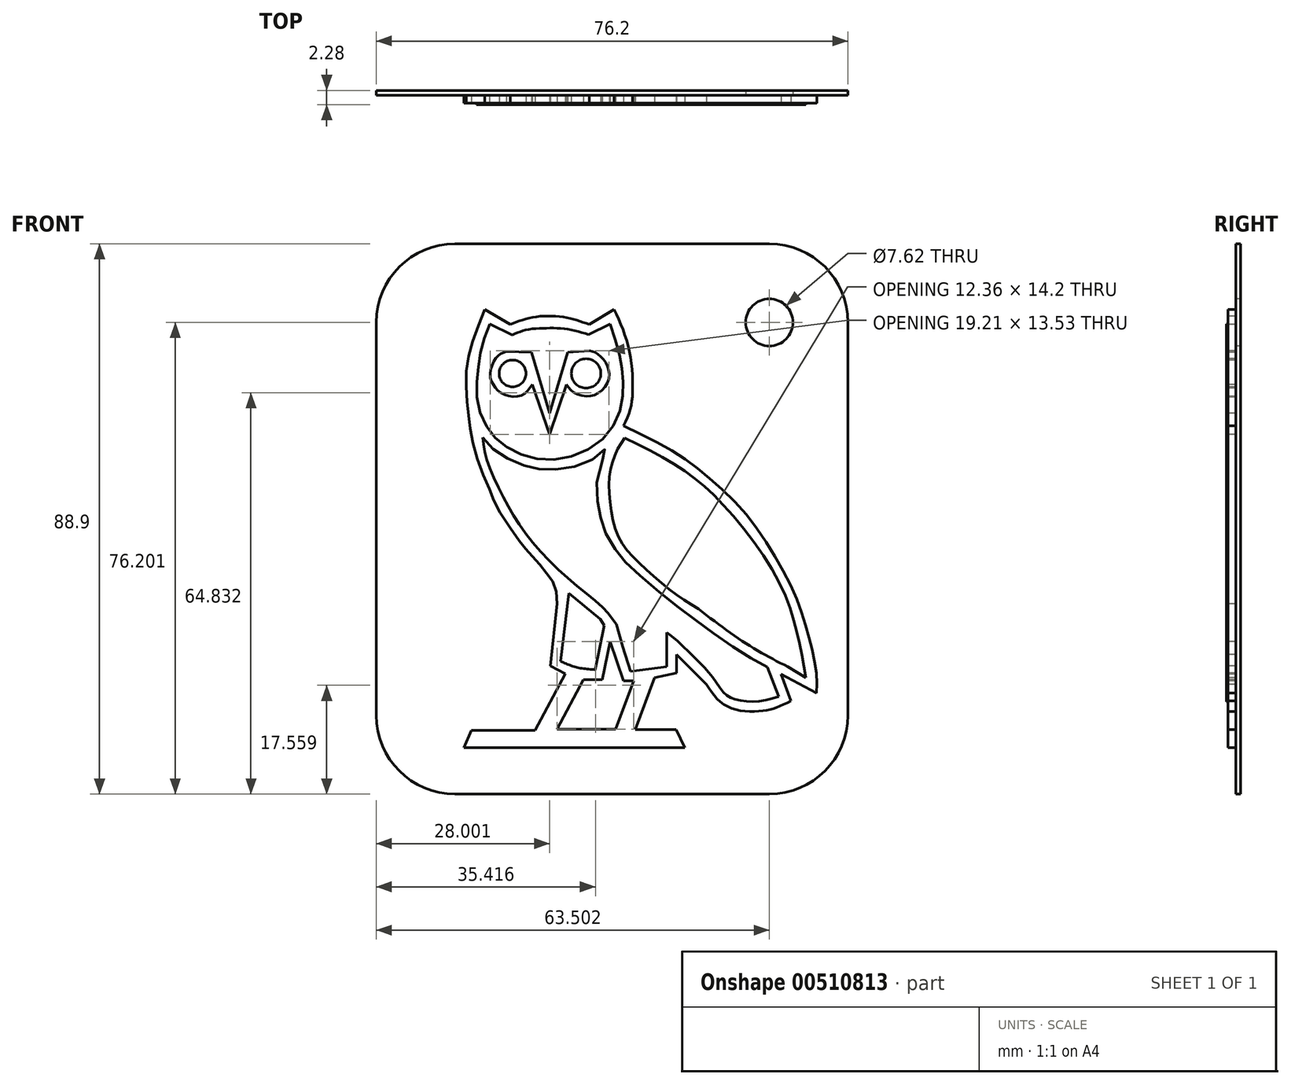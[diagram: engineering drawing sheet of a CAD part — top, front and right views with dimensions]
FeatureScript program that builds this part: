
annotation { "Feature Type Name" : "Feature", "Feature Type Description" : "" }
export const myFeature = defineFeature(function(context is Context, id is Id, definition is map)
    precondition{}
    {
        {
            var Q0;
            Q0=qCreatedBy(makeId("Front.planeOp"),FACE);
            var sketch = newSketch(context, id + "F0", { "sketchPlane" : qUnion([Q0])});
            skLineSegment(sketch, "E0", {"start": v(-23.6, -33.47) * mm, "end": v(12.06, -33.47) * mm});
            skLineSegment(sketch, "E1", {"start": v(12.06, -33.47) * mm, "end": v(10.65, -30.56) * mm});
            skLineSegment(sketch, "E2", {"start": v(10.65, -30.56) * mm, "end": v(4.09, -30.56) * mm});
            skLineSegment(sketch, "E3", {"start": v(4.09, -30.56) * mm, "end": v(7.18, -22.2) * mm});
            skLineSegment(sketch, "E4", {"start": v(7.18, -22.2) * mm, "end": v(10.75, -21.46) * mm});
            skLineSegment(sketch, "E5", {"start": v(10.75, -21.46) * mm, "end": v(10.75, -18.46) * mm});
            skLineSegment(sketch, "E6", {"start": v(10.75, -18.46) * mm, "end": v(15.53, -23.24) * mm});
            skFitSpline(sketch, "E7", {"points": [v(15.53, -23.24) * mm, v(17.79, -26.06) * mm, v(20.88, -27.46) * mm, v(24.54, -27.56) * mm, v(26.7, -27.09) * mm, v(29.23, -25.96) * mm], "startDerivative": vector(9.5, -14.38) * mm, "endDerivative": vector(13.86, 6.72) * mm});
            skLineSegment(sketch, "E8", {"start": v(29.23, -25.96) * mm, "end": v(27.64, -21.65) * mm});
            skLineSegment(sketch, "E9", {"start": v(27.64, -21.65) * mm, "end": v(33.36, -24.65) * mm});
            skFitSpline(sketch, "E10", {"points": [v(33.36, -24.65) * mm, v(33.36, -21.97) * mm, v(32.74, -18.12) * mm, v(31.6, -13.8) * mm, v(29.83, -8.64) * mm, v(26.36, -2.12) * mm, v(21.78, 4.45) * mm, v(15.74, 10.29) * mm, v(10.3, 14.34) * mm, v(2.15, 18.5) * mm], "startDerivative": vector(1.45, 34.65) * mm, "endDerivative": vector(-63.63, 29.95) * mm});
            skLineSegment(sketch, "E11", {"start": v(-3.39, 34.89) * mm, "end": v(0.66, 37.34) * mm});
            skLineSegment(sketch, "E12", {"start": v(0.66, 37.34) * mm, "end": v(-3.39, 34.89) * mm});
            skLineSegment(sketch, "E13", {"start": v(-20.24, 37.34) * mm, "end": v(-16.13, 34.89) * mm});
            skFitSpline(sketch, "E14", {"points": [v(-16.13, 34.89) * mm, v(-12.28, 36.08) * mm, v(-7.17, 36.01) * mm, v(-3.39, 34.89) * mm], "startDerivative": vector(11.3, 4.48) * mm, "endDerivative": vector(11.2, -4.14) * mm});
            skFitSpline(sketch, "E15", {"points": [v(0.66, 37.34) * mm, v(2.36, 33.28) * mm, v(3.44, 28.54) * mm, v(3.63, 23.85) * mm, v(3.25, 21.13) * mm, v(2.15, 18.5) * mm], "startDerivative": vector(8.55, -18.57) * mm, "endDerivative": vector(-7.4, -15.37) * mm});
            skLineSegment(sketch, "E16", {"start": v(-23.6, -33.47) * mm, "end": v(-22.43, -30.72) * mm});
            skLineSegment(sketch, "E17", {"start": v(-22.43, -30.72) * mm, "end": v(-12.15, -30.72) * mm});
            skLineSegment(sketch, "E18", {"start": v(-12.15, -30.72) * mm, "end": v(-7.24, -21.57) * mm});
            skLineSegment(sketch, "E19", {"start": v(-7.24, -21.57) * mm, "end": v(-9.66, -20.27) * mm});
            skLineSegment(sketch, "E20", {"start": v(-9.66, -20.27) * mm, "end": v(-8.53, -10.26) * mm});
            skFitSpline(sketch, "E21", {"points": [v(-8.53, -10.26) * mm, v(-8.96, -7.36) * mm, v(-10.18, -5.38) * mm, v(-11.77, -3.46) * mm, v(-13.41, -1.63) * mm, v(-14.68, 0) * mm, v(-18.09, 5.02) * mm, v(-19.43, 8.09) * mm, v(-21.5, 13.22) * mm, v(-22.6, 18.13) * mm, v(-23.04, 21.93) * mm, v(-23.24, 26.9) * mm, v(-22.37, 31.55) * mm, v(-20.24, 37.34) * mm], "startDerivative": vector(-2.62, 46.1) * mm, "endDerivative": vector(24.41, 61.36) * mm});
            skLineSegment(sketch, "E22", {"start": v(-8.53, -30.52) * mm, "end": v(0.9, -30.52) * mm});
            skLineSegment(sketch, "E23", {"start": v(0.9, -30.52) * mm, "end": v(3.83, -22.7) * mm});
            skLineSegment(sketch, "E24", {"start": v(3.83, -22.7) * mm, "end": v(2.17, -22.7) * mm});
            skLineSegment(sketch, "E25", {"start": v(2.17, -22.7) * mm, "end": v(0, -16.32) * mm});
            skLineSegment(sketch, "E26", {"start": v(0, -16.32) * mm, "end": v(-1.28, -22.5) * mm});
            skLineSegment(sketch, "E27", {"start": v(-1.28, -22.5) * mm, "end": v(-4.33, -22.5) * mm});
            skLineSegment(sketch, "E28", {"start": v(-4.33, -22.5) * mm, "end": v(-8.53, -30.52) * mm});
            skLineSegment(sketch, "E29", {"start": v(-6.68, -8.56) * mm, "end": v(-7.98, -19.53) * mm});
            skFitSpline(sketch, "E30", {"points": [v(-7.98, -19.53) * mm, v(-5.57, -20.48) * mm, v(-2.38, -20.9) * mm], "startDerivative": vector(4.87, -2.28) * mm, "endDerivative": vector(6.31, -0.51) * mm});
            skLineSegment(sketch, "E31", {"start": v(-2.38, -20.9) * mm, "end": v(-0.92, -13.77) * mm});
            skFitSpline(sketch, "E32", {"points": [v(-0.92, -13.77) * mm, v(-1.59, -12.7) * mm], "startDerivative": vector(-0.67, 1.07) * mm, "endDerivative": vector(-0.67, 1.07) * mm});
            skLineSegment(sketch, "E33", {"start": v(-1.59, -12.7) * mm, "end": v(-6.68, -8.56) * mm});
            skFitSpline(sketch, "E34", {"points": [v(-20.57, 16.63) * mm, v(-19.96, 13.17) * mm, v(-17.33, 7.2) * mm, v(-13.65, 1.12) * mm, v(-7.18, -5.8) * mm, v(-0.96, -11.06) * mm, v(1, -13.57) * mm], "startDerivative": vector(2.66, -25.6) * mm, "endDerivative": vector(12.95, -19.83) * mm});
            skLineSegment(sketch, "E35", {"start": v(1, -13.57) * mm, "end": v(2.05, -17.2) * mm});
            skLineSegment(sketch, "E36", {"start": v(2.05, -17.2) * mm, "end": v(3.28, -21.16) * mm});
            skLineSegment(sketch, "E37", {"start": v(3.28, -21.16) * mm, "end": v(9.14, -20.43) * mm});
            skLineSegment(sketch, "E38", {"start": v(9.14, -20.43) * mm, "end": v(9.14, -14.91) * mm});
            skFitSpline(sketch, "E39", {"points": [v(9.14, -14.91) * mm, v(10.49, -15.92) * mm, v(14.08, -19.35) * mm, v(16.72, -22.3) * mm, v(18.53, -24.82) * mm, v(20.26, -25.68) * mm, v(23.4, -26.08) * mm, v(27.22, -25.22) * mm], "startDerivative": vector(11.32, -7.67) * mm, "endDerivative": vector(24.05, 7.52) * mm});
            skLineSegment(sketch, "E40", {"start": v(27.22, -25.22) * mm, "end": v(25.4, -20.47) * mm});
            skFitSpline(sketch, "E41", {"points": [v(25.4, -20.47) * mm, v(20.99, -17.91) * mm, v(15.07, -13.8) * mm, v(10.02, -10.02) * mm, v(3.81, -4.76) * mm, v(1.13, -1.88) * mm, v(-1.02, 1.88) * mm, v(-1.86, 5.4) * mm, v(-2.02, 10.2) * mm, v(-0.74, 14.71) * mm, v(-2.53, 13.26) * mm, v(-7.27, 11.64) * mm, v(-11.23, 11.48) * mm, v(-14.41, 12.31) * mm, v(-18.26, 14.27) * mm, v(-20.57, 16.63) * mm], "startDerivative": vector(-60, 32.93) * mm, "endDerivative": vector(-35.73, 43.8) * mm});
            skFitSpline(sketch, "E42", {"points": [v(2.37, 16.58) * mm, v(11.52, 11.55) * mm, v(18.44, 5.58) * mm, v(26.83, -5.84) * mm, v(30.22, -14.91) * mm, v(31.6, -22.17) * mm], "startDerivative": vector(47.5, -23.94) * mm, "endDerivative": vector(6.94, -41.74) * mm});
            skLineSegment(sketch, "E43", {"start": v(31.6, -22.17) * mm, "end": v(28.72, -20.44) * mm});
            skFitSpline(sketch, "E44", {"points": [v(28.72, -20.44) * mm, v(22.08, -16.74) * mm, v(14.3, -11.1) * mm], "startDerivative": vector(-13.98, 7.2) * mm, "endDerivative": vector(-14.86, 11.39) * mm});
            skLineSegment(sketch, "E45", {"start": v(2.37, 16.58) * mm, "end": v(1.24, 14.74) * mm});
            skFitSpline(sketch, "E46", {"points": [v(1.24, 14.74) * mm, v(0, 11.25) * mm, v(0, 6.33) * mm, v(1.24, 0.79) * mm, v(4.28, -3.24) * mm, v(9.56, -7.89) * mm, v(14.3, -11.1) * mm], "startDerivative": vector(-10.82, -23.88) * mm, "endDerivative": vector(26.87, -17.03) * mm});
            skLineSegment(sketch, "E47", {"start": v(-19.4, 34.97) * mm, "end": v(-15.8, 33.16) * mm});
            skLineSegment(sketch, "E48", {"start": v(0, 34.97) * mm, "end": v(-3.46, 33.24) * mm});
            skFitSpline(sketch, "E49", {"points": [v(-15.8, 33.16) * mm, v(-13.69, 33.99) * mm, v(-10.38, 34.3) * mm, v(-6.92, 34.14) * mm, v(-3.46, 33.24) * mm], "startDerivative": vector(9.22, 4.49) * mm, "endDerivative": vector(12.93, -4.06) * mm});
            skFitSpline(sketch, "E50", {"points": [v(-19.4, 34.97) * mm, v(-20.83, 30.98) * mm, v(-21.36, 27.15) * mm, v(-21.5, 22.86) * mm, v(-20.08, 18.65) * mm, v(-17.6, 15.72) * mm, v(-13.54, 13.61) * mm, v(-8.42, 13.08) * mm, v(-2.86, 15.11) * mm, v(0.83, 19.02) * mm, v(2.03, 23.39) * mm, v(2.03, 26.85) * mm, v(1.43, 30.3) * mm, v(0, 34.97) * mm], "startDerivative": vector(-22.16, -53.18) * mm, "endDerivative": vector(-19.8, 59.83) * mm});
            skLineSegment(sketch, "E51", {"start": v(-9.77, 20.53) * mm, "end": v(-6.82, 30.41) * mm});
            skLineSegment(sketch, "E52", {"start": v(-6.82, 30.41) * mm, "end": v(-9.77, 20.53) * mm});
            skLineSegment(sketch, "E53", {"start": v(-9.77, 17.09) * mm, "end": v(-7.04, 25.18) * mm});
            skFitSpline(sketch, "E54", {"points": [v(-7.04, 25.18) * mm, v(-6.1, 24.08) * mm, v(-3.95, 23.29) * mm, v(-2.04, 23.74) * mm, v(-0.34, 25.62) * mm, v(-0.3, 27.84) * mm, v(-1.2, 29.42) * mm, v(-2.41, 30.36) * mm, v(-3.28, 30.62) * mm], "startDerivative": vector(6.78, -10.36) * mm, "endDerivative": vector(-9.48, 1.96) * mm});
            skLineSegment(sketch, "E55", {"start": v(-3.28, 30.62) * mm, "end": v(-6.82, 30.41) * mm});
            skLineSegment(sketch, "E56", {"start": v(-9.77, 20.53) * mm, "end": v(-12.71, 30.41) * mm});
            skLineSegment(sketch, "E57", {"start": v(-9.77, 17.09) * mm, "end": v(-12.56, 25.18) * mm});
            skCircle(sketch, "E58", {"center": v(-15.76, 26.97) * mm, "radius": 1.62 * mm});
            skCircle(sketch, "E59", {"center": v(-15.76, 26.97) * mm, "radius": 2.17 * mm});
            skFitSpline(sketch, "E60", {"points": [v(-12.56, 25.18) * mm, v(-13.77, 23.75) * mm, v(-15.64, 23.22) * mm, v(-17.75, 23.92) * mm, v(-18.87, 25.18) * mm, v(-19.4, 26.74) * mm, v(-18.75, 28.96) * mm, v(-17.87, 30.01) * mm, v(-16.76, 30.54) * mm], "startDerivative": vector(-8.23, -12.47) * mm, "endDerivative": vector(11.29, 4.29) * mm});
            skCircle(sketch, "E61", {"center": v(-3.87, 26.97) * mm, "radius": 1.74 * mm});
            skCircle(sketch, "E62", {"center": v(-3.87, 26.97) * mm, "radius": 2.38 * mm});
            skLineSegment(sketch, "E63", {"start": v(-16.76, 30.54) * mm, "end": v(-12.71, 30.41) * mm});
            skSolve(sketch);
        }
        {
            var Q0;
            Q0=makeQuery(id+"F0.imprint","IMPRINT",FACE,{"disambiguationData":[TD([[makeQuery(id+"F0.imprint","IMPRINT",EDGE,{"derivedFrom":sQuery(id+"F0.wireOp",EDGE,"E34")}),1.0]])]});
            var Q1;
            Q1=makeQuery(id+"F0.imprint","IMPRINT",FACE,{"disambiguationData":[TD([[makeQuery(id+"F0.imprint","IMPRINT",EDGE,{"derivedFrom":sQuery(id+"F0.wireOp",EDGE,"E0")}),1.0]])]});
            var Q2;
            Q2=makeQuery(id+"F0.imprint","IMPRINT",FACE,{"disambiguationData":[TD([[makeQuery(id+"F0.imprint","IMPRINT",EDGE,{"derivedFrom":sQuery(id+"F0.wireOp",EDGE,"E47")}),-1.0]])]});
            var Q3;
            Q3=makeQuery(id+"F0.imprint","IMPRINT",FACE,{"disambiguationData":[TD([[makeQuery(id+"F0.imprint","IMPRINT",EDGE,{"derivedFrom":sQuery(id+"F0.wireOp",EDGE,"E22")}),1.0]])]});
            var Q4;
            Q4=makeQuery(id+"F0.imprint","IMPRINT",FACE,{"disambiguationData":[TD([[makeQuery(id+"F0.imprint","IMPRINT",EDGE,{"derivedFrom":sQuery(id+"F0.wireOp",EDGE,"E29")}),1.0]])]});
            var Q5;
            Q5=makeQuery(id+"F0.imprint","IMPRINT",FACE,{"disambiguationData":[TD([[makeQuery(id+"F0.imprint","IMPRINT",EDGE,{"derivedFrom":sQuery(id+"F0.wireOp",EDGE,"E42")}),-1.0]])]});
            var Q6;
            Q6=makeQuery(id+"F0.imprint","IMPRINT",FACE,{"disambiguationData":[TD([[makeQuery(id+"F0.imprint","IMPRINT",EDGE,{"derivedFrom":sQuery(id+"F0.wireOp",EDGE,"E61")}),1.0]])]});
            var Q7;
            Q7=makeQuery(id+"F0.imprint","IMPRINT",FACE,{"disambiguationData":[TD([[makeQuery(id+"F0.imprint","IMPRINT",EDGE,{"derivedFrom":sQuery(id+"F0.wireOp",EDGE,"E58")}),1.0]])]});
            var Q8;
            Q8=makeQuery(id+"F0.imprint","IMPRINT",FACE,{"disambiguationData":[TD([[makeQuery(id+"F0.imprint","IMPRINT",EDGE,{"derivedFrom":sQuery(id+"F0.wireOp",EDGE,"E61")}),-1.0]])]});
            var Q9;
            Q9=makeQuery(id+"F0.imprint","IMPRINT",FACE,{"disambiguationData":[TD([[makeQuery(id+"F0.imprint","IMPRINT",EDGE,{"derivedFrom":sQuery(id+"F0.wireOp",EDGE,"E58")}),-1.0]])]});
            extrude(context, id + "F1", {"entities" : qUnion([Q0, Q1, Q2, Q3, Q4, Q5, Q6, Q7, Q8, Q9]), "oppositeDirection" : true, "depth" : 1.27 * mm, "offsetDistance" : 25.4 * mm});
        }
        {
            var Q0;
            Q0=makeQuery(id+"F0.imprint","IMPRINT",FACE,{"disambiguationData":[TD([[makeQuery(id+"F0.imprint","IMPRINT",EDGE,{"derivedFrom":sQuery(id+"F0.wireOp",EDGE,"E34")}),1.0]])]});
            extrude(context, id + "F2", {"entities" : qUnion([Q0]), "operationType" : NewBodyOperationType.ADD, "depth" : 0.25 * mm, "offsetDistance" : 25.4 * mm});
        }
        {
            var Q0;
            Q0=makeQuery(id+"F0.imprint","IMPRINT",FACE,{"disambiguationData":[TD([[makeQuery(id+"F0.imprint","IMPRINT",EDGE,{"derivedFrom":sQuery(id+"F0.wireOp",EDGE,"E42")}),-1.0]])]});
            extrude(context, id + "F3", {"entities" : qUnion([Q0]), "operationType" : NewBodyOperationType.ADD, "depth" : 0.25 * mm, "offsetDistance" : 25.4 * mm});
        }
        {
            var Q0;
            Q0=makeQuery(id+"F0.imprint","IMPRINT",FACE,{"disambiguationData":[TD([[makeQuery(id+"F0.imprint","IMPRINT",EDGE,{"derivedFrom":sQuery(id+"F0.wireOp",EDGE,"E47")}),-1.0]])]});
            extrude(context, id + "F4", {"entities" : qUnion([Q0]), "operationType" : NewBodyOperationType.ADD, "depth" : 0.25 * mm, "offsetDistance" : 25.4 * mm});
        }
        {
            var Q0;
            Q0=makeQuery(id+"F0.imprint","IMPRINT",FACE,{"disambiguationData":[TD([[makeQuery(id+"F0.imprint","IMPRINT",EDGE,{"derivedFrom":sQuery(id+"F0.wireOp",EDGE,"E22")}),1.0]])]});
            extrude(context, id + "F5", {"entities" : qUnion([Q0]), "operationType" : NewBodyOperationType.REMOVE, "oppositeDirection" : true, "depth" : 25.4 * mm, "offsetDistance" : 25.4 * mm});
        }
        {
            var Q0;
            Q0=makeQuery(id+"F0.imprint","IMPRINT",FACE,{"disambiguationData":[TD([[makeQuery(id+"F0.imprint","IMPRINT",EDGE,{"derivedFrom":sQuery(id+"F0.wireOp",EDGE,"E29")}),1.0]])]});
            var Q1;
            Q1=makeQuery(id+"F0.imprint","IMPRINT",FACE,{"disambiguationData":[TD([[makeQuery(id+"F0.imprint","IMPRINT",EDGE,{"derivedFrom":sQuery(id+"F0.wireOp",EDGE,"E34")}),1.0]])]});
            extrude(context, id + "F6", {"entities" : qUnion([Q0, Q1]), "operationType" : NewBodyOperationType.ADD, "depth" : 0.25 * mm, "offsetDistance" : 25.4 * mm});
        }
        {
            var Q0;
            Q0=qCreatedBy(makeId("Front.planeOp"),FACE);
            var sketch = newSketch(context, id + "F7", { "sketchPlane" : qUnion([Q0])});
            skLineSegment(sketch, "E64.bottom", {"start": v(-40.75, 44.98) * mm, "end": v(40.53, 44.98) * mm});
            skLineSegment(sketch, "E64.top", {"start": v(-40.75, -36.3) * mm, "end": v(40.53, -36.3) * mm});
            skLineSegment(sketch, "E64.left", {"start": v(-40.75, 44.98) * mm, "end": v(-40.75, -36.3) * mm});
            skLineSegment(sketch, "E64.right", {"start": v(40.53, 44.98) * mm, "end": v(40.53, -36.3) * mm});
            skSolve(sketch);
        }
        {
            var Q0;
            Q0 = qSketchRegion(id + "F7", true);
            extrude(context, id + "F8", {"entities" : qUnion([Q0]), "depth" : 0.76 * mm, "offsetDistance" : 25.4 * mm});
        }
        {
            var Q0;
            Q0=makeQuery(id+"F8.opExtrude","SWEPT_BODY",BODY,{"disambiguationData":[OSD([sQuery(id+"F7.wireOp",EDGE,"E64.bottom"),sQuery(id+"F7.wireOp",EDGE,"E64.top"),sQuery(id+"F7.wireOp",EDGE,"E64.left"),sQuery(id+"F7.wireOp",EDGE,"E64.right")])]});
            deleteBodies(context, id + "F9", {"entities" : qUnion([Q0])});
        }
        {
            var Q0;
            Q0=makeQuery(id+"F1.opExtrude","CAP_FACE",FACE,{"disambiguationData":[OSD([sQuery(id+"F0.wireOp",EDGE,"E0"),sQuery(id+"F0.wireOp",EDGE,"E1"),sQuery(id+"F0.wireOp",EDGE,"E2"),sQuery(id+"F0.wireOp",EDGE,"E3"),sQuery(id+"F0.wireOp",EDGE,"E4"),sQuery(id+"F0.wireOp",EDGE,"E5"),sQuery(id+"F0.wireOp",EDGE,"E6"),sQuery(id+"F0.wireOp",EDGE,"E7"),sQuery(id+"F0.wireOp",EDGE,"E8"),sQuery(id+"F0.wireOp",EDGE,"E9"),sQuery(id+"F0.wireOp",EDGE,"E10"),sQuery(id+"F0.wireOp",EDGE,"E12"),sQuery(id+"F0.wireOp",EDGE,"E13"),sQuery(id+"F0.wireOp",EDGE,"E14"),sQuery(id+"F0.wireOp",EDGE,"E15"),sQuery(id+"F0.wireOp",EDGE,"E16"),sQuery(id+"F0.wireOp",EDGE,"E17"),sQuery(id+"F0.wireOp",EDGE,"E18"),sQuery(id+"F0.wireOp",EDGE,"E19"),sQuery(id+"F0.wireOp",EDGE,"E20"),sQuery(id+"F0.wireOp",EDGE,"E21"),sQuery(id+"F0.wireOp",EDGE,"E52"),sQuery(id+"F0.wireOp",EDGE,"E53"),sQuery(id+"F0.wireOp",EDGE,"E54"),sQuery(id+"F0.wireOp",EDGE,"E55"),sQuery(id+"F0.wireOp",EDGE,"E56"),sQuery(id+"F0.wireOp",EDGE,"E57"),sQuery(id+"F0.wireOp",EDGE,"E60"),sQuery(id+"F0.wireOp",EDGE,"E63")])],"isStart":false});
            var sketch = newSketch(context, id + "F10", { "sketchPlane" : qUnion([Q0])});
            skLineSegment(sketch, "E65.bottom", {"start": v(-25.73, 47.92) * mm, "end": v(25.07, 47.92) * mm});
            skLineSegment(sketch, "E65.top", {"start": v(-25.73, -40.98) * mm, "end": v(25.07, -40.98) * mm});
            skLineSegment(sketch, "E65.left", {"start": v(-38.43, 35.22) * mm, "end": v(-38.43, -28.28) * mm});
            skLineSegment(sketch, "E65.right", {"start": v(37.77, 35.22) * mm, "end": v(37.77, -28.28) * mm});
            skPoint(sketch, "E66.visualSharp", {"position": v(37.77, 47.92) * mm});
            skArc(sketch, "E66.filletArc", {"start": v(37.77, 35.22) * mm, "mid": v(34.05, 44.2) * mm, "end": v(25.07, 47.92) * mm});
            skPoint(sketch, "E67.visualSharp", {"position": v(-38.43, 47.92) * mm});
            skArc(sketch, "E67.filletArc", {"start": v(-25.73, 47.92) * mm, "mid": v(-34.71, 44.2) * mm, "end": v(-38.43, 35.22) * mm});
            skPoint(sketch, "E68.visualSharp", {"position": v(37.77, -40.98) * mm});
            skArc(sketch, "E68.filletArc", {"start": v(25.07, -40.98) * mm, "mid": v(34.05, -37.26) * mm, "end": v(37.77, -28.28) * mm});
            skPoint(sketch, "E69.visualSharp", {"position": v(-38.43, -40.98) * mm});
            skArc(sketch, "E69.filletArc", {"start": v(-38.43, -28.28) * mm, "mid": v(-34.71, -37.26) * mm, "end": v(-25.73, -40.98) * mm});
            skSolve(sketch);
        }
        {
            var Q0;
            Q0 = qSketchRegion(id + "F10", true);
            extrude(context, id + "F11", {"entities" : qUnion([Q0]), "depth" : 0.76 * mm, "offsetDistance" : 25.4 * mm});
        }
        {
            var Q0;
            Q0=makeQuery(id+"F11.opExtrude","CAP_FACE",FACE,{"disambiguationData":[OSD([sQuery(id+"F10.wireOp",EDGE,"E65.bottom"),sQuery(id+"F10.wireOp",EDGE,"E65.top"),sQuery(id+"F10.wireOp",EDGE,"E65.left"),sQuery(id+"F10.wireOp",EDGE,"E65.right"),sQuery(id+"F10.wireOp",EDGE,"E66.filletArc"),sQuery(id+"F10.wireOp",EDGE,"E67.filletArc"),sQuery(id+"F10.wireOp",EDGE,"E68.filletArc"),sQuery(id+"F10.wireOp",EDGE,"E69.filletArc")])],"isStart":true});
            var sketch = newSketch(context, id + "F12", { "sketchPlane" : qUnion([Q0])});
            skCircle(sketch, "E70", {"center": v(25.73, 35.22) * mm, "radius": 3.81 * mm});
            skSolve(sketch);
        }
        {
            var Q0;
            Q0 = qSketchRegion(id + "F12", true);
            extrude(context, id + "F13", {"entities" : qUnion([Q0]), "operationType" : NewBodyOperationType.REMOVE, "oppositeDirection" : true, "depth" : 25.4 * mm, "offsetDistance" : 25.4 * mm});
        }
    });
